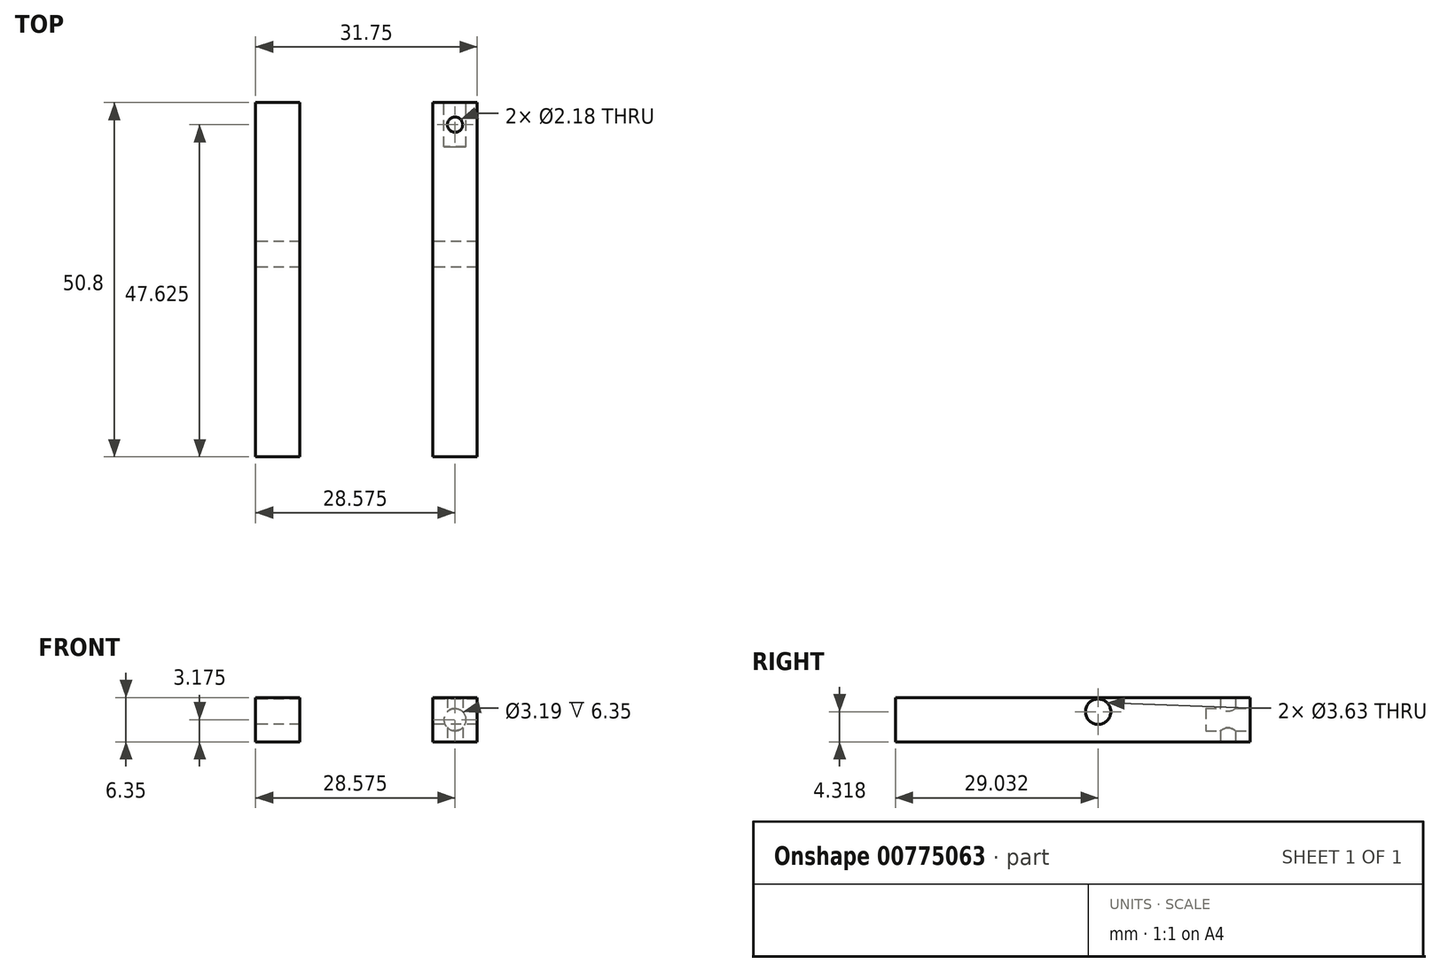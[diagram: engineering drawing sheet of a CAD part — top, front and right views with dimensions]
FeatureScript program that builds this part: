
annotation { "Feature Type Name" : "Feature", "Feature Type Description" : "" }
export const myFeature = defineFeature(function(context is Context, id is Id, definition is map)
    precondition{}
    {
        {
            var Q0;
            Q0=qCreatedBy(makeId("Front.planeOp"),FACE);
            var sketch = newSketch(context, id + "F0", { "sketchPlane" : qUnion([Q0])});
            skLineSegment(sketch, "E0.bottom", {"start": v(0, 0) * mm, "end": v(6.35, 0) * mm});
            skLineSegment(sketch, "E0.top", {"start": v(0, 6.35) * mm, "end": v(6.35, 6.35) * mm});
            skLineSegment(sketch, "E0.left", {"start": v(0, 0) * mm, "end": v(0, 6.35) * mm});
            skLineSegment(sketch, "E0.right", {"start": v(6.35, 0) * mm, "end": v(6.35, 6.35) * mm});
            skSolve(sketch);
        }
        {
            var Q0;
            Q0 = qSketchRegion(id + "F0", true);
            extrude(context, id + "F1", {"entities" : qUnion([Q0]), "depth" : 50.8 * mm, "offsetDistance" : 25.4 * mm});
        }
        {
            var Q0;
            Q0=makeQuery(id+"F1.opExtrude","SWEPT_FACE",FACE,{"disambiguationData":[OSD([sQuery(id+"F0.wireOp",EDGE,"E0.left")])]});
            var sketch = newSketch(context, id + "F2", { "sketchPlane" : qUnion([Q0])});
            skCircle(sketch, "E1", {"center": v(21.77, 4.32) * mm, "radius": 1.82 * mm});
            skSolve(sketch);
        }
        {
            var Q0;
            Q0 = qSketchRegion(id + "F2", true);
            extrude(context, id + "F3", {"entities" : qUnion([Q0]), "operationType" : NewBodyOperationType.REMOVE, "endBound" : BoundingType.UP_TO_NEXT, "oppositeDirection" : true, "depth" : 25.4 * mm, "offsetDistance" : 25.4 * mm});
        }
        {
            var Q0;
            Q0=makeQuery(id+"F1.opExtrude","SWEPT_BODY",BODY,{"disambiguationData":[OSD([sQuery(id+"F0.wireOp",EDGE,"E0.bottom"),sQuery(id+"F0.wireOp",EDGE,"E0.top"),sQuery(id+"F0.wireOp",EDGE,"E0.left"),sQuery(id+"F0.wireOp",EDGE,"E0.right")])]});
            transform(context, id + "F4", {"entities" : qUnion([Q0]), "transformType" : TransformType.TRANSLATION_3D, "dx" : 25.4 * mm, "dy" : 0 * mm, "dz" : 0 * mm, "makeCopy" : true});
        }
        {
            var Q0;
            Q0=makeQuery(id+"F4.opPattern","COPY",FACE,{"derivedFrom":makeQuery(id+"F1.opExtrude","CAP_FACE",FACE,{"disambiguationData":[OSD([sQuery(id+"F0.wireOp",EDGE,"E0.bottom"),sQuery(id+"F0.wireOp",EDGE,"E0.top"),sQuery(id+"F0.wireOp",EDGE,"E0.left"),sQuery(id+"F0.wireOp",EDGE,"E0.right")])],"isStart":true}),"instanceName":"1"});
            var sketch = newSketch(context, id + "F5", { "sketchPlane" : qUnion([Q0])});
            skCircle(sketch, "E2", {"center": v(-28.58, 3.18) * mm, "radius": 1.6 * mm});
            skSolve(sketch);
        }
        {
            var Q0;
            Q0 = qSketchRegion(id + "F5", true);
            extrude(context, id + "F6", {"entities" : qUnion([Q0]), "operationType" : NewBodyOperationType.REMOVE, "oppositeDirection" : true, "depth" : 6.35 * mm, "offsetDistance" : 25.4 * mm});
        }
        {
            var Q0;
            Q0=makeQuery(id+"F4.opPattern","COPY",FACE,{"derivedFrom":makeQuery(id+"F1.opExtrude","SWEPT_FACE",FACE,{"disambiguationData":[OSD([sQuery(id+"F0.wireOp",EDGE,"E0.bottom")])]}),"instanceName":"1"});
            var sketch = newSketch(context, id + "F7", { "sketchPlane" : qUnion([Q0])});
            skCircle(sketch, "E3", {"center": v(-40.22, -233.82) * mm, "radius": 118.52 * mm});
            skCircle(sketch, "E4", {"center": v(28.57, 3.17) * mm, "radius": 1.1 * mm});
            skSolve(sketch);
        }
        {
            var Q0;
            Q0=makeQuery(id+"F7.imprint","IMPRINT",FACE,{"disambiguationData":[TD([[makeQuery(id+"F7.imprint","IMPRINT",EDGE,{"derivedFrom":sQuery(id+"F7.wireOp",EDGE,"E3")}),1.0]])]});
            var Q1;
            Q1=makeQuery(id+"F7.imprint","IMPRINT",FACE,{"disambiguationData":[TD([[makeQuery(id+"F7.imprint","IMPRINT",EDGE,{"derivedFrom":sQuery(id+"F7.wireOp",EDGE,"E4")}),1.0]])]});
            extrude(context, id + "F8", {"entities" : qUnion([Q0, Q1]), "operationType" : NewBodyOperationType.REMOVE, "oppositeDirection" : true, "depth" : 25.4 * mm, "offsetDistance" : 25.4 * mm});
        }
    });
